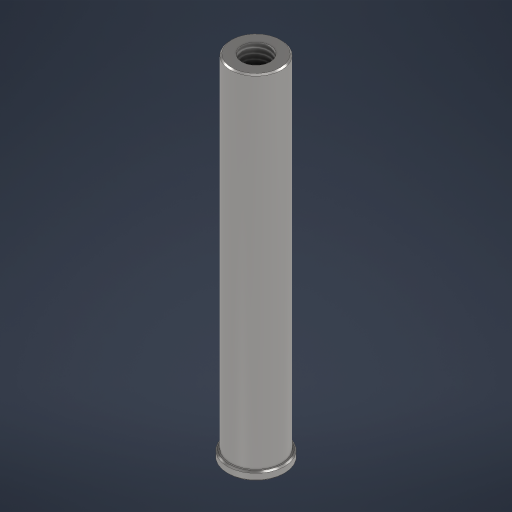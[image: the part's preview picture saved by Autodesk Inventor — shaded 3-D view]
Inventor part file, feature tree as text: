
AUTODESK INVENTOR PART (.ipt)
format: ipt  version: 2025 (Build 290162010, 162A)  size: 196,096 bytes
history: native  units: mm
features: extrude x3, chamfer x2, thread x1
ambient origin geometry x8: Origin, YZ Plane, XZ Plane, XY Plane, X Axis, Y Axis, Z Axis, Center Point
bodies: Solid1 (feature_tree)
feature tree (6):
  extrude  "Extrusion1"  Depth=5.0mm
  chamfer  "Chamfer1"  Distance=0.75mm
  extrude  "Extrusion2"  Depth=0.125mm TaperAngle=45.0deg
  extrude  "Extrusion3"  Depth=4.5mm
  thread  "Thread1"  [1 undecoded]
  chamfer  "Chamfer2"  Distance=2.5mm
note: 1 required parameter value undecoded (feature->parameter linkage not recoverable at this tier; creation-order binding heuristic only, values carry confidence <= 0.55)
